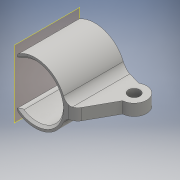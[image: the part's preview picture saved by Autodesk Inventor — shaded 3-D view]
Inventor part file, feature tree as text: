
AUTODESK INVENTOR PART (.ipt)
format: ipt  version: 2016 (Build 200138000, 138)  size: 171,008 bytes
history: native  units: mm
features: fillet x6, extrude x2, chamfer x2, sketch x2, plane x1, split x1
ambient origin geometry x8: Origin, YZ Plane, XZ Plane, XY Plane, X Axis, Y Axis, Z Axis, Center Point
bodies: Solid1 (feature_tree)
feature tree (14):
  extrude  "Extrusion1"  Depth=3.0mm
  extrude  "Extrusion2"  Depth=3.0mm
  plane  "Work Plane1"
  split  "Split1"
  chamfer  "Chamfer1"  Distance=27.0mm
  chamfer  "Chamfer2"  Distance=40.0mm
  fillet  "Fillet1"  Radius=6.0mm
  fillet  "Fillet2"  Radius=16.7mm
  fillet  "Fillet3"  Radius=17.0mm
  fillet  "Fillet4"  Radius=7.65mm
  fillet  "Fillet5"  Radius=40.0mm
  fillet  "Fillet6"  [1 undecoded]
  sketch  "Sketch1"  dims[d0=35.0mm d1=3.0mm]
  sketch  "Sketch2"  dims[d2=7.75mm d3=3.875mm d4=27.0mm d5=40.0mm d6=0.0mm d10=6.0mm d14=16.7mm d15=17.0mm d16=7.65mm d17=40.0mm d18=0.0mm d19=-12.0mm d20=1.5mm d21=2.0mm d22=45.0deg d23=1.5mm d24=2.0mm d25=45.0deg d26=6.0mm d27=6.0mm d28=6.0mm d29=3.0mm d30=3.0mm d31=3.0mm]
note: 1 required parameter value undecoded (feature->parameter linkage not recoverable at this tier; creation-order binding heuristic only, values carry confidence <= 0.55)
